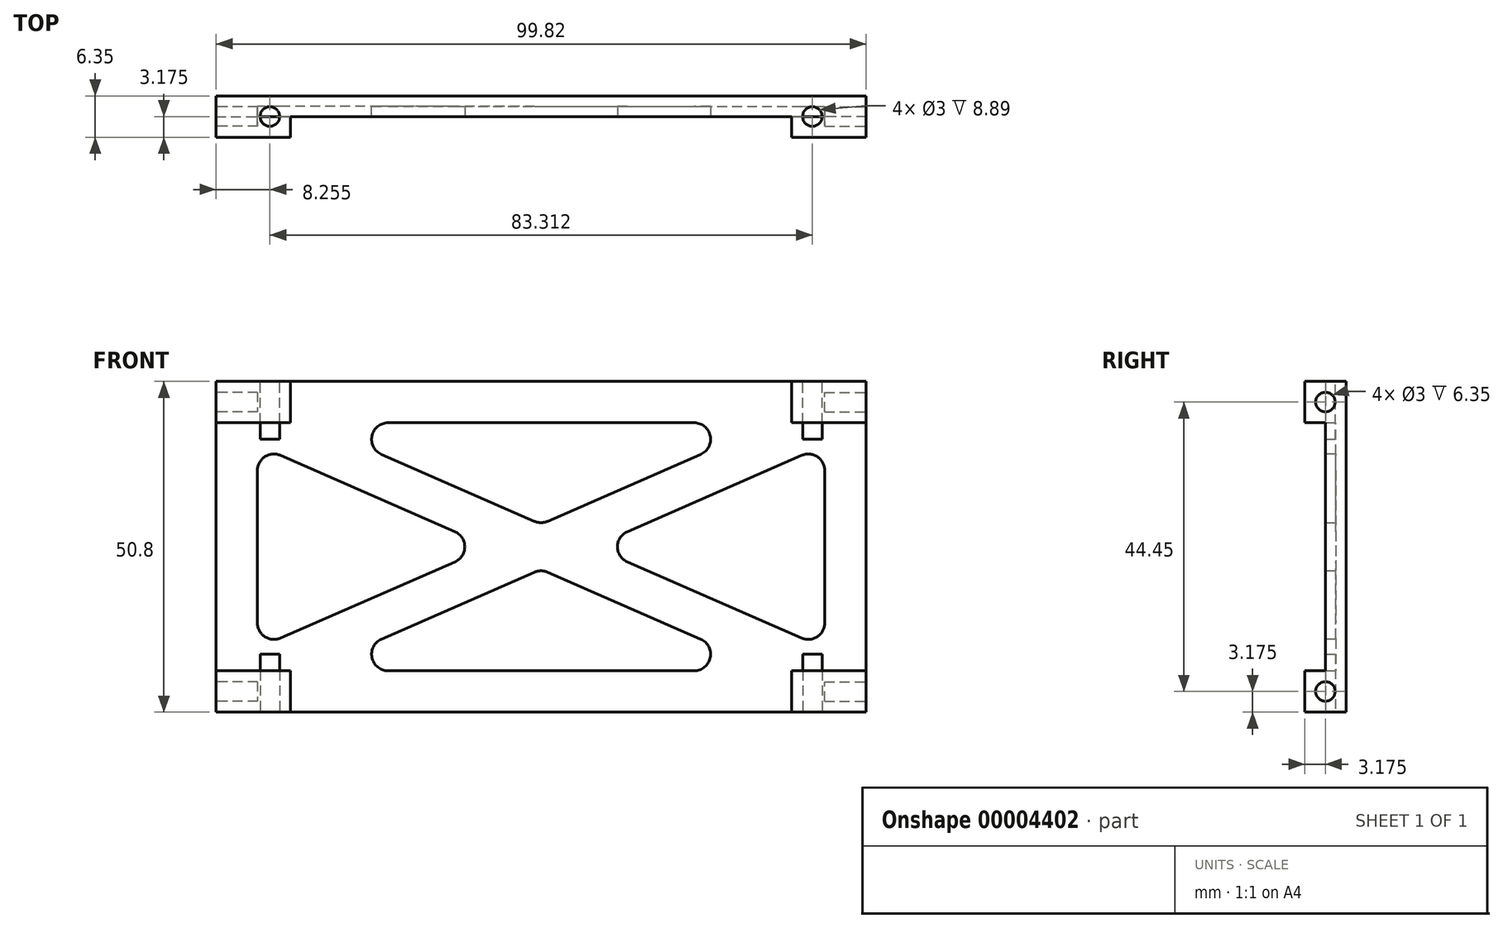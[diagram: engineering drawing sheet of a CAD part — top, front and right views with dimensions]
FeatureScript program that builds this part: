
annotation { "Feature Type Name" : "Feature", "Feature Type Description" : "" }
export const myFeature = defineFeature(function(context is Context, id is Id, definition is map)
    precondition{}
    {
        {
            var Q0;
            Q0=qCreatedBy(makeId("Front.planeOp"),FACE);
            var sketch = newSketch(context, id + "F0", { "sketchPlane" : qUnion([Q0])});
            skLineSegment(sketch, "E0.bottom", {"start": v(0, 0) * mm, "end": v(99.82, 0) * mm});
            skLineSegment(sketch, "E0.top", {"start": v(0, 50.8) * mm, "end": v(99.82, 50.8) * mm});
            skLineSegment(sketch, "E0.left", {"start": v(0, 0) * mm, "end": v(0, 50.8) * mm});
            skLineSegment(sketch, "E0.right", {"start": v(99.82, 0) * mm, "end": v(99.82, 50.8) * mm});
            skSolve(sketch);
        }
        {
            var Q0;
            Q0=makeQuery(id+"F0.imprint","IMPRINT",FACE,{"disambiguationData":[TD([[makeQuery(id+"F0.imprint","IMPRINT",EDGE,{"derivedFrom":sQuery(id+"F0.wireOp",EDGE,"E0.bottom")}),1.0]])]});
            extrude(context, id + "F1", {"entities" : qUnion([Q0]), "depth" : 1.59 * mm});
        }
        {
            var Q0;
            Q0=makeQuery(id+"F1.opExtrude","CAP_FACE",FACE,{"disambiguationData":[OSD([sQuery(id+"F0.wireOp",EDGE,"E0.bottom"),sQuery(id+"F0.wireOp",EDGE,"E0.top"),sQuery(id+"F0.wireOp",EDGE,"E0.left"),sQuery(id+"F0.wireOp",EDGE,"E0.right")])],"isStart":false});
            var sketch = newSketch(context, id + "F2", { "sketchPlane" : qUnion([Q0])});
            skLineSegment(sketch, "E1.bottom", {"start": v(0, 50.8) * mm, "end": v(99.82, 50.8) * mm});
            skLineSegment(sketch, "E1.top", {"start": v(0, 0) * mm, "end": v(99.82, 0) * mm});
            skLineSegment(sketch, "E1.left", {"start": v(0, 50.8) * mm, "end": v(0, 0) * mm});
            skLineSegment(sketch, "E1.right", {"start": v(99.82, 50.8) * mm, "end": v(99.82, 0) * mm});
            skLineSegment(sketch, "E2.0", {"start": v(14.27, 44.45) * mm, "end": v(85.55, 44.45) * mm});
            skLineSegment(sketch, "E2.1", {"start": v(6.35, 40.98) * mm, "end": v(6.35, 9.82) * mm});
            skLineSegment(sketch, "E2.2", {"start": v(14.27, 6.35) * mm, "end": v(85.55, 6.35) * mm});
            skLineSegment(sketch, "E2.3", {"start": v(93.47, 40.98) * mm, "end": v(93.47, 9.82) * mm});
            skLineSegment(sketch, "E3", {"start": v(6.35, 6.35) * mm, "end": v(93.47, 44.45) * mm, "construction": true});
            skLineSegment(sketch, "E4", {"start": v(93.47, 6.35) * mm, "end": v(6.35, 44.45) * mm, "construction": true});
            skLineSegment(sketch, "E5.0", {"start": v(93.47, 9.82) * mm, "end": v(57.84, 25.4) * mm});
            skLineSegment(sketch, "E6.0", {"start": v(14.27, 6.35) * mm, "end": v(49.91, 21.93) * mm});
            skLineSegment(sketch, "E7.0", {"start": v(6.35, 9.82) * mm, "end": v(41.99, 25.4) * mm});
            skLineSegment(sketch, "E8.0", {"start": v(85.55, 6.35) * mm, "end": v(49.91, 21.93) * mm});
            skLineSegment(sketch, "E9.trimOffspring", {"start": v(49.91, 28.87) * mm, "end": v(14.27, 44.45) * mm});
            skLineSegment(sketch, "E10.trimOffspring", {"start": v(57.84, 25.4) * mm, "end": v(93.47, 40.98) * mm});
            skLineSegment(sketch, "E11.trimOffspring", {"start": v(41.99, 25.4) * mm, "end": v(6.35, 40.98) * mm});
            skLineSegment(sketch, "E12.trimOffspring", {"start": v(49.91, 28.87) * mm, "end": v(85.55, 44.45) * mm});
            skSolve(sketch);
        }
        {
            var Q0;
            Q0=makeQuery(id+"F2.imprint","IMPRINT",FACE,{"disambiguationData":[TD([[makeQuery(id+"F2.imprint","IMPRINT",EDGE,{"derivedFrom":sQuery(id+"F2.wireOp",EDGE,"E1.bottom")}),-1.0]])]});
            extrude(context, id + "F3", {"entities" : qUnion([Q0]), "operationType" : NewBodyOperationType.ADD, "depth" : 1.59 * mm});
        }
        {
            var Q0;
            Q0=makeQuery(id+"F3.opExtrude","SWEPT_EDGE",EDGE,{"disambiguationData":[OSD([sQuery(id+"F2.wireOp",EDGE,"E2.0"),sQuery(id+"F2.wireOp",EDGE,"E9.trimOffspring")])]});
            var Q1;
            Q1=makeQuery(id+"F3.opExtrude","SWEPT_EDGE",EDGE,{"disambiguationData":[OSD([sQuery(id+"F2.wireOp",EDGE,"E5.0"),sQuery(id+"F2.wireOp",EDGE,"E10.trimOffspring")])]});
            var Q2;
            Q2=makeQuery(id+"F3.opExtrude","SWEPT_EDGE",EDGE,{"disambiguationData":[OSD([sQuery(id+"F2.wireOp",EDGE,"E9.trimOffspring"),sQuery(id+"F2.wireOp",EDGE,"E12.trimOffspring")])]});
            var Q3;
            Q3=makeQuery(id+"F3.opExtrude","SWEPT_EDGE",EDGE,{"disambiguationData":[OSD([sQuery(id+"F2.wireOp",EDGE,"E2.1"),sQuery(id+"F2.wireOp",EDGE,"E7.0")])]});
            var Q4;
            Q4=makeQuery(id+"F3.opExtrude","SWEPT_EDGE",EDGE,{"disambiguationData":[OSD([sQuery(id+"F2.wireOp",EDGE,"E6.0"),sQuery(id+"F2.wireOp",EDGE,"E8.0")])]});
            var Q5;
            Q5=makeQuery(id+"F3.opExtrude","SWEPT_EDGE",EDGE,{"disambiguationData":[OSD([sQuery(id+"F2.wireOp",EDGE,"E2.1"),sQuery(id+"F2.wireOp",EDGE,"E11.trimOffspring")])]});
            var Q6;
            Q6=makeQuery(id+"F3.opExtrude","SWEPT_EDGE",EDGE,{"disambiguationData":[OSD([sQuery(id+"F2.wireOp",EDGE,"E2.3"),sQuery(id+"F2.wireOp",EDGE,"E10.trimOffspring")])]});
            var Q7;
            Q7=makeQuery(id+"F3.opExtrude","SWEPT_EDGE",EDGE,{"disambiguationData":[OSD([sQuery(id+"F2.wireOp",EDGE,"E7.0"),sQuery(id+"F2.wireOp",EDGE,"E11.trimOffspring")])]});
            var Q8;
            Q8=makeQuery(id+"F3.opExtrude","SWEPT_EDGE",EDGE,{"disambiguationData":[OSD([sQuery(id+"F2.wireOp",EDGE,"E2.0"),sQuery(id+"F2.wireOp",EDGE,"E12.trimOffspring")])]});
            var Q9;
            Q9=makeQuery(id+"F3.opExtrude","SWEPT_EDGE",EDGE,{"disambiguationData":[OSD([sQuery(id+"F2.wireOp",EDGE,"E2.3"),sQuery(id+"F2.wireOp",EDGE,"E5.0")])]});
            var Q10;
            Q10=makeQuery(id+"F3.opExtrude","SWEPT_EDGE",EDGE,{"disambiguationData":[OSD([sQuery(id+"F2.wireOp",EDGE,"E2.2"),sQuery(id+"F2.wireOp",EDGE,"E8.0")])]});
            var Q11;
            Q11=makeQuery(id+"F3.opExtrude","SWEPT_EDGE",EDGE,{"disambiguationData":[OSD([sQuery(id+"F2.wireOp",EDGE,"E2.2"),sQuery(id+"F2.wireOp",EDGE,"E6.0")])]});
            fillet(context, id + "F4", {"entities" : qUnion([Q0, Q1, Q2, Q3, Q4, Q5, Q6, Q7, Q8, Q9, Q10, Q11]), "radius" : 2.54 * mm, "tangentPropagation" : true, "allowEdgeOverflow" : false});
        }
        {
            var Q0;
            Q0=makeQuery(id+"F3.opExtrude","CAP_FACE",FACE,{"disambiguationData":[OSD([sQuery(id+"F2.wireOp",EDGE,"E1.bottom"),sQuery(id+"F2.wireOp",EDGE,"E1.top"),sQuery(id+"F2.wireOp",EDGE,"E1.left"),sQuery(id+"F2.wireOp",EDGE,"E1.right"),sQuery(id+"F2.wireOp",EDGE,"E2.0"),sQuery(id+"F2.wireOp",EDGE,"E2.1"),sQuery(id+"F2.wireOp",EDGE,"E2.2"),sQuery(id+"F2.wireOp",EDGE,"E2.3"),sQuery(id+"F2.wireOp",EDGE,"E5.0"),sQuery(id+"F2.wireOp",EDGE,"E6.0"),sQuery(id+"F2.wireOp",EDGE,"E7.0"),sQuery(id+"F2.wireOp",EDGE,"E8.0"),sQuery(id+"F2.wireOp",EDGE,"E9.trimOffspring"),sQuery(id+"F2.wireOp",EDGE,"E10.trimOffspring"),sQuery(id+"F2.wireOp",EDGE,"E11.trimOffspring"),sQuery(id+"F2.wireOp",EDGE,"E12.trimOffspring")])],"isStart":false});
            var sketch = newSketch(context, id + "F5", { "sketchPlane" : qUnion([Q0])});
            skLineSegment(sketch, "E13.bottom", {"start": v(0, 50.8) * mm, "end": v(11.43, 50.8) * mm});
            skLineSegment(sketch, "E13.top", {"start": v(0, 44.45) * mm, "end": v(11.43, 44.45) * mm});
            skLineSegment(sketch, "E13.left", {"start": v(0, 50.8) * mm, "end": v(0, 44.45) * mm});
            skLineSegment(sketch, "E14.bottom", {"start": v(0, 0) * mm, "end": v(11.43, 0) * mm});
            skLineSegment(sketch, "E14.top", {"start": v(0, 6.35) * mm, "end": v(11.43, 6.35) * mm});
            skLineSegment(sketch, "E14.left", {"start": v(0, 0) * mm, "end": v(0, 6.35) * mm});
            skLineSegment(sketch, "E15.bottom", {"start": v(99.82, 0) * mm, "end": v(88.4, 0) * mm});
            skLineSegment(sketch, "E15.top", {"start": v(99.82, 6.35) * mm, "end": v(88.4, 6.35) * mm});
            skLineSegment(sketch, "E15.left", {"start": v(99.82, 0) * mm, "end": v(99.82, 6.35) * mm});
            skLineSegment(sketch, "E16.bottom", {"start": v(99.82, 50.8) * mm, "end": v(88.4, 50.8) * mm});
            skLineSegment(sketch, "E16.top", {"start": v(99.82, 44.45) * mm, "end": v(88.4, 44.45) * mm});
            skLineSegment(sketch, "E16.left", {"start": v(99.82, 50.8) * mm, "end": v(99.82, 44.45) * mm});
            skLineSegment(sketch, "E17", {"start": v(11.43, 50.8) * mm, "end": v(11.43, 44.45) * mm});
            skLineSegment(sketch, "E18", {"start": v(88.4, 50.8) * mm, "end": v(88.4, 44.45) * mm});
            skLineSegment(sketch, "E19", {"start": v(88.4, 6.35) * mm, "end": v(88.4, 0) * mm});
            skLineSegment(sketch, "E20", {"start": v(11.43, 6.35) * mm, "end": v(11.43, 0) * mm});
            skSolve(sketch);
        }
        {
            var Q0;
            Q0 = qSketchRegion(id + "F5", true);
            extrude(context, id + "F6", {"entities" : qUnion([Q0]), "operationType" : NewBodyOperationType.ADD, "depth" : 3.17 * mm});
        }
        {
            var Q0;
            Q0=makeQuery(id+"F6.boolean.opBoolean","MERGE",FACE,{"derivedFrom":[makeQuery(id+"F3.boolean.opBoolean","MERGE",FACE,{"derivedFrom":[makeQuery(id+"F1.opExtrude","SWEPT_FACE",FACE,{"disambiguationData":[OSD([sQuery(id+"F0.wireOp",EDGE,"E0.bottom")])]}),makeQuery(id+"F3.opExtrude","SWEPT_FACE",FACE,{"disambiguationData":[OSD([sQuery(id+"F2.wireOp",EDGE,"E1.top")])]})]}),makeQuery(id+"F6.opExtrude","SWEPT_FACE",FACE,{"disambiguationData":[OSD([sQuery(id+"F5.wireOp",EDGE,"E14.bottom")])]}),makeQuery(id+"F6.opExtrude","SWEPT_FACE",FACE,{"disambiguationData":[OSD([sQuery(id+"F5.wireOp",EDGE,"E15.bottom")])]})]});
            var sketch = newSketch(context, id + "F7", { "sketchPlane" : qUnion([Q0])});
            skCircle(sketch, "E21", {"center": v(8.26, 3.17) * mm, "radius": 1.5 * mm});
            skCircle(sketch, "E22", {"center": v(91.57, 3.17) * mm, "radius": 1.5 * mm});
            skLineSegment(sketch, "E23", {"start": v(8.26, 3.17) * mm, "end": v(91.57, 3.17) * mm, "construction": true});
            skLineSegment(sketch, "E24", {"start": v(0, 3.17) * mm, "end": v(8.26, 3.17) * mm, "construction": true});
            skSolve(sketch);
        }
        {
            var Q0;
            Q0 = qSketchRegion(id + "F7", true);
            extrude(context, id + "F8", {"entities" : qUnion([Q0]), "operationType" : NewBodyOperationType.REMOVE, "oppositeDirection" : true, "depth" : 8.9 * mm});
        }
        {
            var Q0;
            Q0=makeQuery(id+"F6.boolean.opBoolean","MERGE",FACE,{"derivedFrom":[makeQuery(id+"F3.boolean.opBoolean","MERGE",FACE,{"derivedFrom":[makeQuery(id+"F1.opExtrude","SWEPT_FACE",FACE,{"disambiguationData":[OSD([sQuery(id+"F0.wireOp",EDGE,"E0.left")])]}),makeQuery(id+"F3.opExtrude","SWEPT_FACE",FACE,{"disambiguationData":[OSD([sQuery(id+"F2.wireOp",EDGE,"E1.left")])]})]}),makeQuery(id+"F6.opExtrude","SWEPT_FACE",FACE,{"disambiguationData":[OSD([sQuery(id+"F5.wireOp",EDGE,"E13.left")])]}),makeQuery(id+"F6.opExtrude","SWEPT_FACE",FACE,{"disambiguationData":[OSD([sQuery(id+"F5.wireOp",EDGE,"E14.left")])]})]});
            var sketch = newSketch(context, id + "F9", { "sketchPlane" : qUnion([Q0])});
            skCircle(sketch, "E25", {"center": v(3.17, 47.63) * mm, "radius": 1.5 * mm});
            skCircle(sketch, "E26", {"center": v(3.17, 3.18) * mm, "radius": 1.5 * mm});
            skLineSegment(sketch, "E27", {"start": v(3.17, 47.63) * mm, "end": v(3.17, 3.18) * mm, "construction": true});
            skLineSegment(sketch, "E28", {"start": v(3.17, 3.18) * mm, "end": v(3.17, 0) * mm, "construction": true});
            skSolve(sketch);
        }
        {
            var Q0;
            Q0 = qSketchRegion(id + "F9", true);
            extrude(context, id + "F10", {"entities" : qUnion([Q0]), "operationType" : NewBodyOperationType.REMOVE, "oppositeDirection" : true, "depth" : 6.35 * mm});
        }
        {
            var Q0;
            Q0=makeQuery(id+"F6.boolean.opBoolean","MERGE",FACE,{"derivedFrom":[makeQuery(id+"F3.boolean.opBoolean","MERGE",FACE,{"derivedFrom":[makeQuery(id+"F1.opExtrude","SWEPT_FACE",FACE,{"disambiguationData":[OSD([sQuery(id+"F0.wireOp",EDGE,"E0.top")])]}),makeQuery(id+"F3.opExtrude","SWEPT_FACE",FACE,{"disambiguationData":[OSD([sQuery(id+"F2.wireOp",EDGE,"E1.bottom")])]})]}),makeQuery(id+"F6.opExtrude","SWEPT_FACE",FACE,{"disambiguationData":[OSD([sQuery(id+"F5.wireOp",EDGE,"E13.bottom")])]}),makeQuery(id+"F6.opExtrude","SWEPT_FACE",FACE,{"disambiguationData":[OSD([sQuery(id+"F5.wireOp",EDGE,"E16.bottom")])]})]});
            var sketch = newSketch(context, id + "F11", { "sketchPlane" : qUnion([Q0])});
            skCircle(sketch, "E29", {"center": v(91.57, -3.17) * mm, "radius": 1.5 * mm});
            skCircle(sketch, "E30", {"center": v(8.26, -3.17) * mm, "radius": 1.5 * mm});
            skLineSegment(sketch, "E31", {"start": v(91.57, -3.17) * mm, "end": v(8.26, -3.17) * mm, "construction": true});
            skLineSegment(sketch, "E32", {"start": v(8.26, -3.17) * mm, "end": v(0, -3.17) * mm, "construction": true});
            skSolve(sketch);
        }
        {
            var Q0;
            Q0 = qSketchRegion(id + "F11", true);
            extrude(context, id + "F12", {"entities" : qUnion([Q0]), "operationType" : NewBodyOperationType.REMOVE, "oppositeDirection" : true, "depth" : 8.9 * mm});
        }
        {
            var Q0;
            Q0=makeQuery(id+"F6.boolean.opBoolean","MERGE",FACE,{"derivedFrom":[makeQuery(id+"F3.boolean.opBoolean","MERGE",FACE,{"derivedFrom":[makeQuery(id+"F1.opExtrude","SWEPT_FACE",FACE,{"disambiguationData":[OSD([sQuery(id+"F0.wireOp",EDGE,"E0.right")])]}),makeQuery(id+"F3.opExtrude","SWEPT_FACE",FACE,{"disambiguationData":[OSD([sQuery(id+"F2.wireOp",EDGE,"E1.right")])]})]}),makeQuery(id+"F6.opExtrude","SWEPT_FACE",FACE,{"disambiguationData":[OSD([sQuery(id+"F5.wireOp",EDGE,"E15.left")])]}),makeQuery(id+"F6.opExtrude","SWEPT_FACE",FACE,{"disambiguationData":[OSD([sQuery(id+"F5.wireOp",EDGE,"E16.left")])]})]});
            var sketch = newSketch(context, id + "F13", { "sketchPlane" : qUnion([Q0])});
            skCircle(sketch, "E33", {"center": v(-3.18, 3.17) * mm, "radius": 1.5 * mm});
            skCircle(sketch, "E34", {"center": v(-3.18, 47.62) * mm, "radius": 1.5 * mm});
            skLineSegment(sketch, "E35", {"start": v(-3.18, 3.17) * mm, "end": v(-3.18, 47.62) * mm, "construction": true});
            skLineSegment(sketch, "E36", {"start": v(-3.18, 47.62) * mm, "end": v(-3.18, 50.8) * mm, "construction": true});
            skSolve(sketch);
        }
        {
            var Q0;
            Q0 = qSketchRegion(id + "F13", true);
            extrude(context, id + "F14", {"entities" : qUnion([Q0]), "operationType" : NewBodyOperationType.REMOVE, "oppositeDirection" : true, "depth" : 6.35 * mm});
        }
    });
